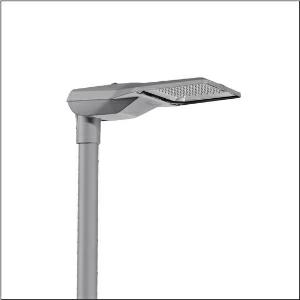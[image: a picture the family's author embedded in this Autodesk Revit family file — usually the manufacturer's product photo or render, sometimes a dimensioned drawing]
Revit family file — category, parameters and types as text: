
# Revit family: streetlight_sl_21_midi___pl52_5xe3h33s08mb_0b8e
name_source: partatom
category: Lighting Fixtures
units: mm (PartAtom-declared; Revit-internal decimal feet)

## family parameters
Cut with Voids When Loaded = No
Host = Face
Light Source = No
Part Type = Normal
Room Calculation Point = No
Round Connector Dimension = Use Diameter
Shared = No

## types (1)
- --- (1 x LED, 17960 lm, 136 W, 3000K)
    Apparent Load = 136 VA
    CIE Flux Codes = 27 59 98 100 100
    Color Rendering = 70
    Color Temperature = 3000K
    Default Elevation = 1800 mm
    Description = Streetlight SL 21 midi, mast luminaire, primary light control with lens, of PMMA, primary optical cover: cover, of toughened safety glass, transparent, light distribution: PL52, light emission: direct distribution, primary light characteristic: asymmetric, installation type: side-entry, post-top, LED, High Power LED, rated luminous flux: 17.960lm, luminous efficacy: 132lm/W, light colour: 730, colour temperature: 3000K, control: overheat protection, constant luminous flux control, time-dependent luminous flux control, flexible luminous flux parameterisation, presetting dimming logarithmic, mains connection: 230..240V, AC, 50/60Hz, start of lifetime: 136W, end of service life: 142W, reduction: 61W, luminaire housing, of diecast aluminium, powder-coated, Siteco® metallic grey (DB 702S), corrosivity category C5 mid according to DIN EN ISO 12944, please order mast flange separately, inclination adjustable: 0°, 5°, 10°, 15°, sealing non-destructively replaceable, multi-level sealing system, length: 644mm, width: 335mm, height: 110mm, mast flange for spigot size: 42mm (side-entry): 5XC10008XM4, 60/48mm (side-entry/post-top): 5XC10108XM2, 76/60mm (side-entry/post-top): 5XC10108XM1, Smart Interface above, protection rating (complete): IP66, insulation class (complete): insulation class II (safety insulation), certification: CE, ENEC, ENEC+, VDE, impact resistance: IK09, permissible operating ambient temperature for outdoor applications: -40..+50°C, standard-compliant lighting for roads and squares, packaging unit: 1 piece

Light Distribution: PL52
    Height = 111 mm
    Lamp = 1 x LED
    Lamp Light Flux = 17960 lm
    Lamp Power = 136 W
    Lamp count = 1
    Length = 644 mm
    Luminous efficacy = 132 lm/W
    Manufacturer = Siteco
    ModVariant = No
    Model = 5XE3H33S08MB
    Number of Poles = 1
    OnlyDefault = Yes
    Power Factor = 1
    Product Name = Streetlight SL 21 midi | PL52
    Product group = mast luminaire | pylon top
    ProductGroupID = 6100
    Protection Class = Protection class II
    Protection Degree = IP 66
    RLX_Detail_Level = 1
    RLX_Emergency_Light_Flux = 0 lm
    RLX_Emergency_Type = 0
    RLX_Emergency_Type_DB = No
    RlxData = <blob elided: 100181 chars, md5=cb78d4c1>
    Socket = socket
    Standby Power = 0 W
    System Light Flux = 17960 lm
    System Power = 136 W
    Type Comments = factory setting: luminous flux: 100 % | dim-lin: 254 | 695 mA
    Type Image = l_1004302.jpg
    URL = http://relux.com
    VarID = @adj_124733
    Voltage = 0 V
    Weight = 0.00 kg
    Width = 336 mm

## geometry (parser evidence)
native form markers: Blend x4, Sweep x12
no freeform markers — native parametric forms only
